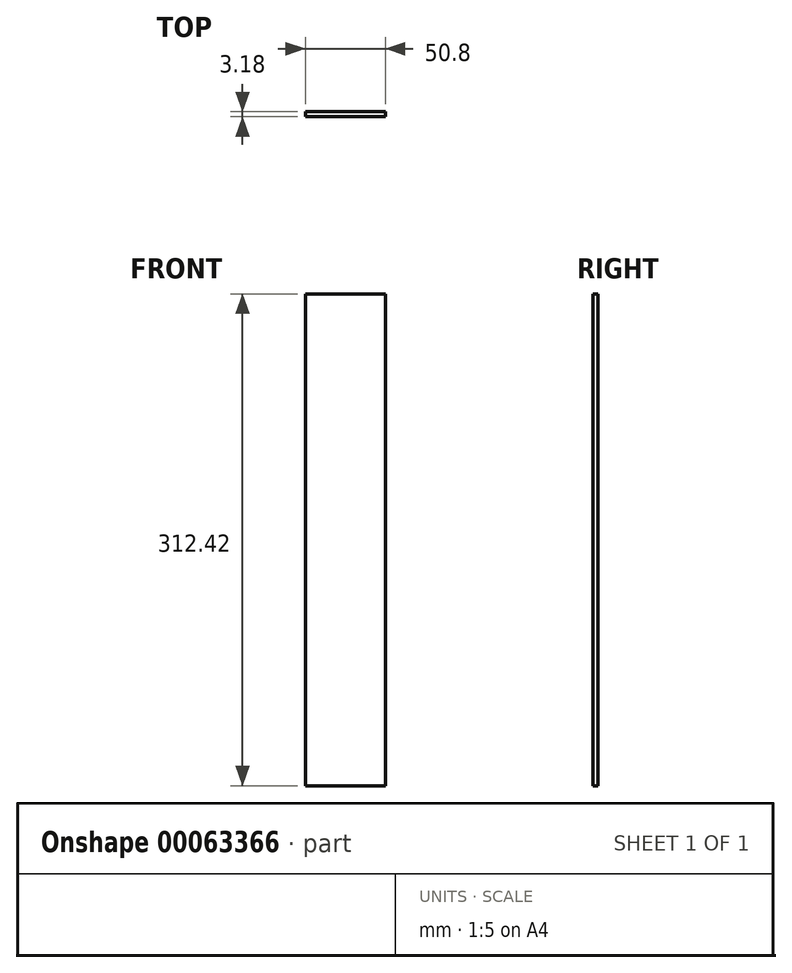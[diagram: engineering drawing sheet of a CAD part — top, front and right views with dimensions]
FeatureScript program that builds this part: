
annotation { "Feature Type Name" : "Feature", "Feature Type Description" : "" }
export const myFeature = defineFeature(function(context is Context, id is Id, definition is map)
    precondition{}
    {
        {
            var Q0;
            Q0=qCreatedBy(makeId("Front.planeOp"),FACE);
            var sketch = newSketch(context, id + "F0", { "sketchPlane" : qUnion([Q0])});
            skLineSegment(sketch, "E0.rect.bottom", {"start": v(25.4, 156.21) * mm, "end": v(-25.4, 156.21) * mm});
            skLineSegment(sketch, "E0.rect.top", {"start": v(25.4, -156.21) * mm, "end": v(-25.4, -156.21) * mm});
            skLineSegment(sketch, "E0.rect.left", {"start": v(25.4, 156.21) * mm, "end": v(25.4, -156.21) * mm});
            skLineSegment(sketch, "E0.rect.right", {"start": v(-25.4, 156.21) * mm, "end": v(-25.4, -156.21) * mm});
            skPoint(sketch, "E0.rect.middle", {"position": v(0, 0) * mm});
            skSolve(sketch);
        }
        {
            var Q0;
            Q0=makeQuery(id+"F0.imprint","IMPRINT",FACE,{"disambiguationData":[TD([[makeQuery(id+"F0.imprint","IMPRINT",EDGE,{"derivedFrom":sQuery(id+"F0.wireOp",EDGE,"E0.rect.bottom")}),1.0]])]});
            extrude(context, id + "F1", {"entities" : qUnion([Q0]), "endBound" : BoundingType.SYMMETRIC, "depth" : 3.17 * mm});
        }
    });
